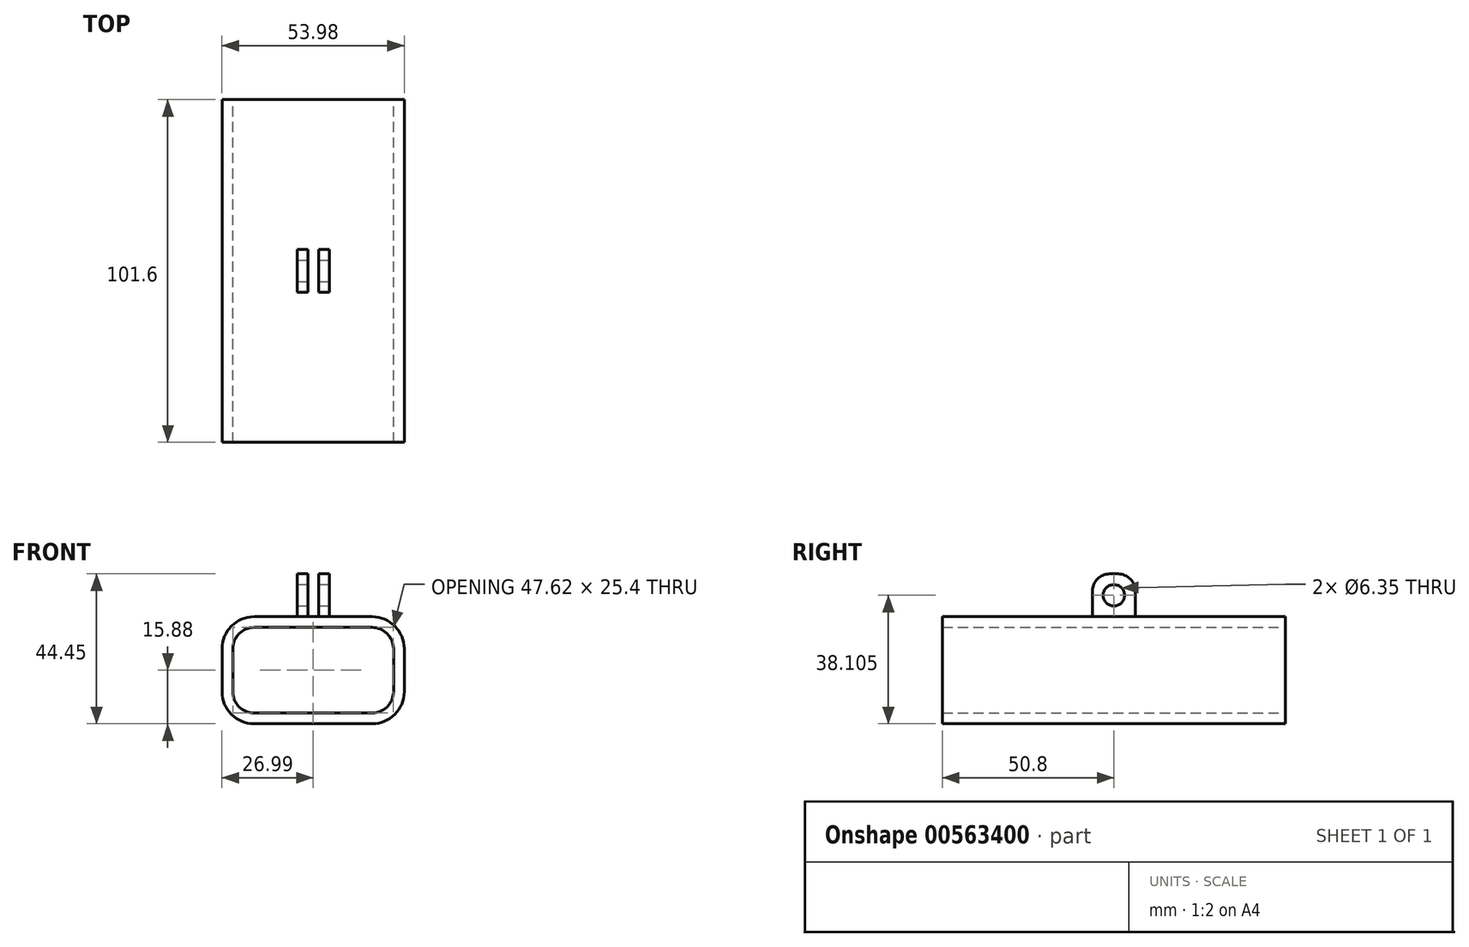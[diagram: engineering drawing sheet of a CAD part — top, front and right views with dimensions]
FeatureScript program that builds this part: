
annotation { "Feature Type Name" : "Feature", "Feature Type Description" : "" }
export const myFeature = defineFeature(function(context is Context, id is Id, definition is map)
    precondition{}
    {
        {
            var Q0;
            Q0=qCreatedBy(makeId("Front.planeOp"),FACE);
            var sketch = newSketch(context, id + "F0", { "sketchPlane" : qUnion([Q0])});
            skLineSegment(sketch, "E0.bottom", {"start": v(-17.46, 12.7) * mm, "end": v(17.46, 12.7) * mm});
            skLineSegment(sketch, "E0.top", {"start": v(-17.46, -12.7) * mm, "end": v(17.46, -12.7) * mm});
            skLineSegment(sketch, "E0.left", {"start": v(-23.81, 6.35) * mm, "end": v(-23.81, -6.35) * mm});
            skLineSegment(sketch, "E0.right", {"start": v(23.81, 6.35) * mm, "end": v(23.81, -6.35) * mm});
            skPoint(sketch, "E0.middle", {"position": v(0, 0) * mm});
            skLineSegment(sketch, "E1.0", {"start": v(-17.46, 15.88) * mm, "end": v(17.46, 15.88) * mm});
            skLineSegment(sketch, "E1.1", {"start": v(-26.99, 6.35) * mm, "end": v(-26.99, -6.35) * mm});
            skLineSegment(sketch, "E1.2", {"start": v(-17.46, -15.88) * mm, "end": v(17.46, -15.88) * mm});
            skLineSegment(sketch, "E1.3", {"start": v(26.99, 6.35) * mm, "end": v(26.99, -6.35) * mm});
            skArc(sketch, "E2.filletArc", {"start": v(-17.46, 12.7) * mm, "mid": v(-21.95, 10.84) * mm, "end": v(-23.81, 6.35) * mm});
            skArc(sketch, "E3.filletArc", {"start": v(-23.81, -6.35) * mm, "mid": v(-21.95, -10.84) * mm, "end": v(-17.46, -12.7) * mm});
            skArc(sketch, "E4.filletArc", {"start": v(17.46, -12.7) * mm, "mid": v(21.95, -10.84) * mm, "end": v(23.81, -6.35) * mm});
            skArc(sketch, "E5.filletArc", {"start": v(23.81, 6.35) * mm, "mid": v(21.95, 10.84) * mm, "end": v(17.46, 12.7) * mm});
            skArc(sketch, "E6.0", {"start": v(-17.46, 15.88) * mm, "mid": v(-24.2, 13.09) * mm, "end": v(-26.99, 6.35) * mm});
            skArc(sketch, "E7.0", {"start": v(26.99, 6.35) * mm, "mid": v(24.2, 13.09) * mm, "end": v(17.46, 15.88) * mm});
            skArc(sketch, "E8.0", {"start": v(-26.99, -6.35) * mm, "mid": v(-24.2, -13.09) * mm, "end": v(-17.46, -15.87) * mm});
            skArc(sketch, "E9.0", {"start": v(17.46, -15.88) * mm, "mid": v(24.2, -13.09) * mm, "end": v(26.99, -6.35) * mm});
            skSolve(sketch);
        }
        {
            var Q0;
            Q0=makeQuery(id+"F0.imprint","IMPRINT",FACE,{"disambiguationData":[TD([[makeQuery(id+"F0.imprint","IMPRINT",EDGE,{"derivedFrom":sQuery(id+"F0.wireOp",EDGE,"E0.bottom")}),1.0]])]});
            extrude(context, id + "F1", {"entities" : qUnion([Q0]), "depth" : 101.6 * mm, "offsetDistance" : 25.4 * mm});
        }
        {
            var Q0;
            Q0=makeQuery(id+"F1.opExtrude","SWEPT_FACE",FACE,{"disambiguationData":[OSD([sQuery(id+"F0.wireOp",EDGE,"E1.0")])]});
            var sketch = newSketch(context, id + "F2", { "sketchPlane" : qUnion([Q0])});
            skLineSegment(sketch, "E10.bottom", {"start": v(-4.76, -44.45) * mm, "end": v(-1.59, -44.45) * mm});
            skLineSegment(sketch, "E10.top", {"start": v(-4.76, -57.15) * mm, "end": v(-1.59, -57.15) * mm});
            skLineSegment(sketch, "E10.left", {"start": v(-4.76, -44.45) * mm, "end": v(-4.76, -57.15) * mm});
            skLineSegment(sketch, "E10.right", {"start": v(-1.59, -44.45) * mm, "end": v(-1.59, -57.15) * mm});
            skLineSegment(sketch, "E11.MirrorCS", {"start": v(1.59, -44.45) * mm, "end": v(1.59, -57.15) * mm});
            skLineSegment(sketch, "E12.MirrorCS", {"start": v(4.76, -44.45) * mm, "end": v(1.59, -44.45) * mm});
            skLineSegment(sketch, "E13.MirrorCS", {"start": v(4.76, -44.45) * mm, "end": v(4.76, -57.15) * mm});
            skLineSegment(sketch, "E14.MirrorCS", {"start": v(4.76, -57.15) * mm, "end": v(1.59, -57.15) * mm});
            skSolve(sketch);
        }
        {
            var Q0;
            Q0=makeQuery(id+"F2.imprint","IMPRINT",FACE,{"disambiguationData":[TD([[makeQuery(id+"F2.imprint","IMPRINT",EDGE,{"derivedFrom":sQuery(id+"F2.wireOp",EDGE,"E10.bottom")}),-1.0]])]});
            var Q1;
            Q1=makeQuery(id+"F2.imprint","IMPRINT",FACE,{"disambiguationData":[TD([[makeQuery(id+"F2.imprint","IMPRINT",EDGE,{"derivedFrom":sQuery(id+"F2.wireOp",EDGE,"E11.MirrorCS")}),1.0]])]});
            extrude(context, id + "F3", {"entities" : qUnion([Q0, Q1]), "operationType" : NewBodyOperationType.ADD, "depth" : 12.7 * mm, "offsetDistance" : 25.4 * mm});
        }
        {
            var Q0;
            Q0=makeQuery(id+"F3.opExtrude","SWEPT_FACE",FACE,{"disambiguationData":[OSD([sQuery(id+"F2.wireOp",EDGE,"E13.MirrorCS")])]});
            var sketch = newSketch(context, id + "F4", { "sketchPlane" : qUnion([Q0])});
            skPoint(sketch, "E15", {"position": v(-50.8, 22.23) * mm});
            skSolve(sketch);
        }
        {
            var Q0;
            Q0=sQuery(id+"F4.wireOp",VERTEX,"E15");
            var Q1;
            Q1=makeQuery(id+"F1.opExtrude","SWEPT_BODY",BODY,{"disambiguationData":[OSD([sQuery(id+"F0.wireOp",EDGE,"E0.bottom"),sQuery(id+"F0.wireOp",EDGE,"E0.top"),sQuery(id+"F0.wireOp",EDGE,"E0.left"),sQuery(id+"F0.wireOp",EDGE,"E0.right"),sQuery(id+"F0.wireOp",EDGE,"E1.0"),sQuery(id+"F0.wireOp",EDGE,"E1.1"),sQuery(id+"F0.wireOp",EDGE,"E1.2"),sQuery(id+"F0.wireOp",EDGE,"E1.3"),sQuery(id+"F0.wireOp",EDGE,"e3dd6d84-a1cc-4fc8-82bd-8036cdaaac70.filletArc"),sQuery(id+"F0.wireOp",EDGE,"c572dc0c-529b-4c9b-8d07-5c0cc57df01f.filletArc"),sQuery(id+"F0.wireOp",EDGE,"2677b0f4-ca84-4b21-83da-852043f086e9.filletArc"),sQuery(id+"F0.wireOp",EDGE,"a0ecfc47-e7d9-4acb-9cfd-d0d7ad91326c.filletArc")])]});
            hole(context, id + "F5", {"style" : HoleStyle.SIMPLE, "endStyle" : HoleEndStyle.THROUGH, "holeDiameter" : 6.35 * mm, "isTappedThrough" : true, "tappedDepth" : 12.7 * mm, "tapClearance" : 3, "locations" : qUnion([Q0]), "scope" : qUnion([Q1])});
        }
        {
            var Q0;
            Q0=makeQuery(id+"F3.opExtrude","CAP_EDGE",EDGE,{"disambiguationData":[OSD([sQuery(id+"F2.wireOp",EDGE,"E10.top")])],"isStart":false});
            var Q1;
            Q1=makeQuery(id+"F3.opExtrude","CAP_EDGE",EDGE,{"disambiguationData":[OSD([sQuery(id+"F2.wireOp",EDGE,"E14.MirrorCS")])],"isStart":false});
            var Q2;
            Q2=makeQuery(id+"F3.opExtrude","CAP_EDGE",EDGE,{"disambiguationData":[OSD([sQuery(id+"F2.wireOp",EDGE,"E12.MirrorCS")])],"isStart":false});
            var Q3;
            Q3=makeQuery(id+"F3.opExtrude","CAP_EDGE",EDGE,{"disambiguationData":[OSD([sQuery(id+"F2.wireOp",EDGE,"E10.bottom")])],"isStart":false});
            fillet(context, id + "F6", {"entities" : qUnion([Q0, Q1, Q2, Q3]), "radius" : 5.08 * mm, "tangentPropagation" : true, "allowEdgeOverflow" : false});
        }
    });
